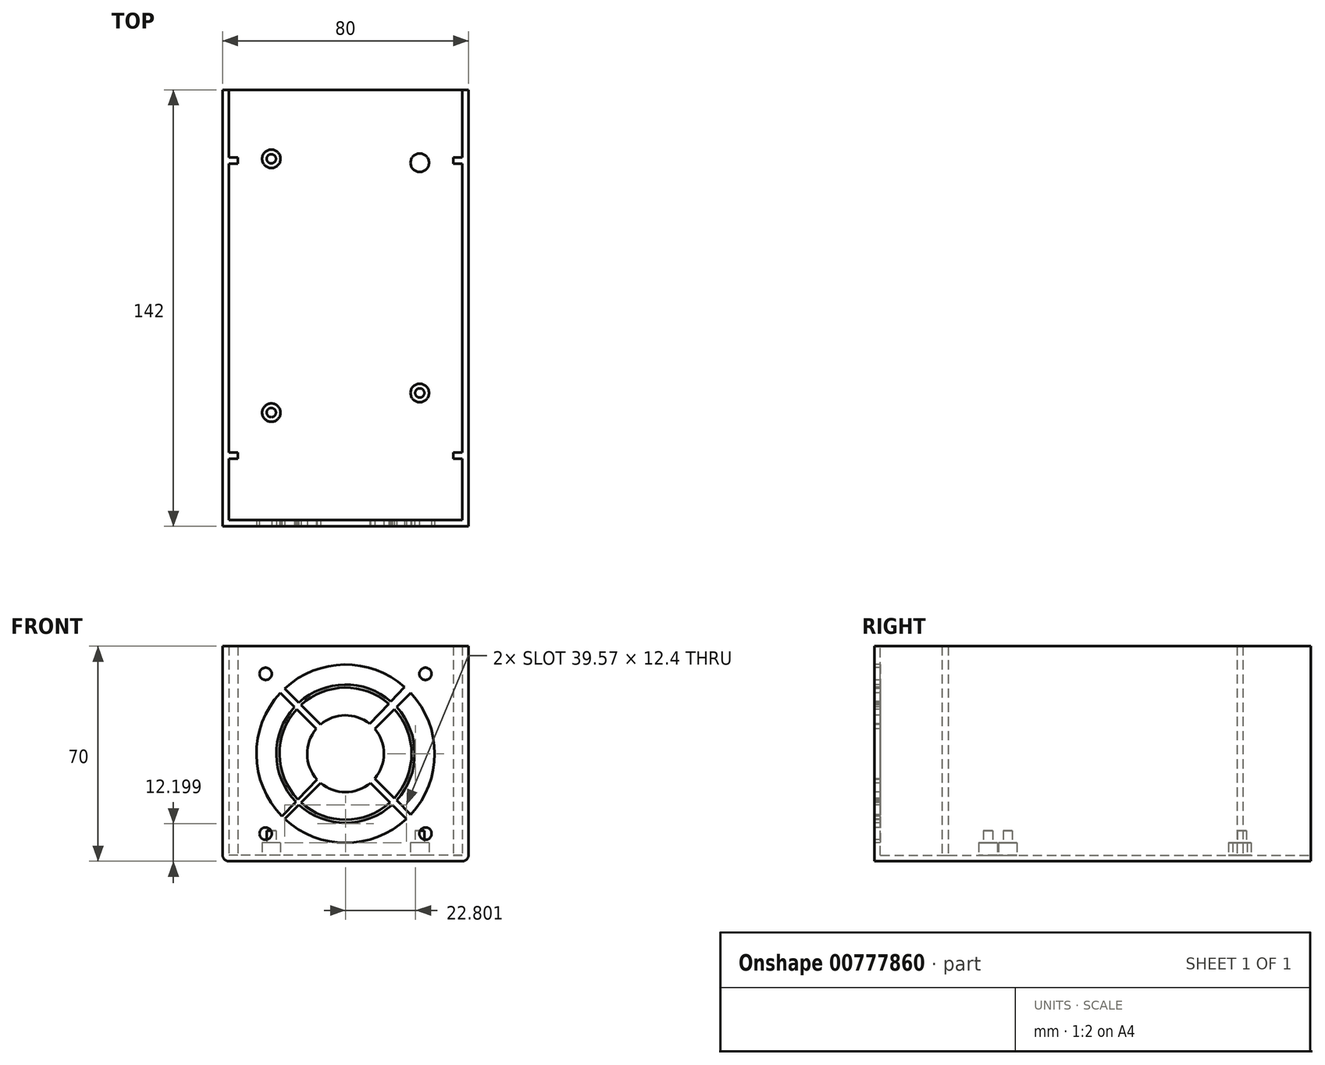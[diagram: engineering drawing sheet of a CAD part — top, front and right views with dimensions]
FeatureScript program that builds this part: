
annotation { "Feature Type Name" : "Feature", "Feature Type Description" : "" }
export const myFeature = defineFeature(function(context is Context, id is Id, definition is map)
    precondition{}
    {
        {
            var Q0;
            Q0=qCreatedBy(makeId("Front.planeOp"),FACE);
            var sketch = newSketch(context, id + "F0", { "sketchPlane" : qUnion([Q0])});
            skLineSegment(sketch, "E0.bottom", {"start": v(-40, 0) * mm, "end": v(40, 0) * mm});
            skLineSegment(sketch, "E0.top", {"start": v(-40, 70) * mm, "end": v(40, 70) * mm});
            skLineSegment(sketch, "E0.left", {"start": v(-40, 0) * mm, "end": v(-40, 70) * mm});
            skLineSegment(sketch, "E0.right", {"start": v(40, 0) * mm, "end": v(40, 70) * mm});
            skPoint(sketch, "E0.middle", {"position": v(0, 35) * mm});
            skSolve(sketch);
        }
        {
            var Q0;
            Q0 = qSketchRegion(id + "F0", true);
            extrude(context, id + "F1", {"entities" : qUnion([Q0]), "depth" : 2 * mm, "offsetDistance" : 25 * mm});
        }
        {
            var Q0;
            Q0=qCreatedBy(makeId("Top.planeOp"),FACE);
            var sketch = newSketch(context, id + "F2", { "sketchPlane" : qUnion([Q0])});
            skLineSegment(sketch, "E1.bottom", {"start": v(40, 0) * mm, "end": v(-40, 0) * mm});
            skLineSegment(sketch, "E1.top", {"start": v(40, 140) * mm, "end": v(-40, 140) * mm});
            skLineSegment(sketch, "E1.left", {"start": v(40, 0) * mm, "end": v(40, 140) * mm});
            skLineSegment(sketch, "E1.right", {"start": v(-40, 0) * mm, "end": v(-40, 140) * mm});
            skPoint(sketch, "E1.middle", {"position": v(0, 70) * mm});
            skSolve(sketch);
        }
        {
            var Q0;
            Q0 = qSketchRegion(id + "F2", true);
            extrude(context, id + "F3", {"entities" : qUnion([Q0]), "operationType" : NewBodyOperationType.ADD, "depth" : 2 * mm, "offsetDistance" : 25 * mm});
        }
        {
            var Q0;
            Q0=makeQuery(id+"F3.boolean.opBoolean","MERGE",FACE,{"derivedFrom":[makeQuery(id+"F1.opExtrude","SWEPT_FACE",FACE,{"disambiguationData":[OSD([sQuery(id+"F0.wireOp",EDGE,"E0.left")])]}),makeQuery(id+"F3.opExtrude","SWEPT_FACE",FACE,{"disambiguationData":[OSD([sQuery(id+"F2.wireOp",EDGE,"E1.right")])]})]});
            var sketch = newSketch(context, id + "F4", { "sketchPlane" : qUnion([Q0])});
            skLineSegment(sketch, "E2.bottom", {"start": v(-140, 2) * mm, "end": v(0, 2) * mm});
            skLineSegment(sketch, "E2.top", {"start": v(-140, 70) * mm, "end": v(0, 70) * mm});
            skLineSegment(sketch, "E2.left", {"start": v(-140, 2) * mm, "end": v(-140, 70) * mm});
            skLineSegment(sketch, "E2.right", {"start": v(0, 2) * mm, "end": v(0, 70) * mm});
            skSolve(sketch);
        }
        {
            var Q0;
            Q0=makeQuery(id+"F4.imprint","IMPRINT",FACE,{"disambiguationData":[TD([[makeQuery(id+"F4.imprint","IMPRINT",EDGE,{"derivedFrom":sQuery(id+"F4.wireOp",EDGE,"E2.bottom")}),-1.0]])]});
            extrude(context, id + "F5", {"entities" : qUnion([Q0]), "operationType" : NewBodyOperationType.ADD, "oppositeDirection" : true, "depth" : 2 * mm, "offsetDistance" : 25 * mm});
        }
        {
            var Q0;
            Q0=makeQuery(id+"F3.boolean.opBoolean","MERGE",FACE,{"derivedFrom":[makeQuery(id+"F1.opExtrude","SWEPT_FACE",FACE,{"disambiguationData":[OSD([sQuery(id+"F0.wireOp",EDGE,"E0.right")])]}),makeQuery(id+"F3.opExtrude","SWEPT_FACE",FACE,{"disambiguationData":[OSD([sQuery(id+"F2.wireOp",EDGE,"E1.left")])]})]});
            var sketch = newSketch(context, id + "F6", { "sketchPlane" : qUnion([Q0])});
            skLineSegment(sketch, "E3.bottom", {"start": v(140, 2) * mm, "end": v(0, 2) * mm});
            skLineSegment(sketch, "E3.top", {"start": v(140, 70) * mm, "end": v(0, 70) * mm});
            skLineSegment(sketch, "E3.left", {"start": v(140, 2) * mm, "end": v(140, 70) * mm});
            skLineSegment(sketch, "E3.right", {"start": v(0, 2) * mm, "end": v(0, 70) * mm});
            skSolve(sketch);
        }
        {
            var Q0;
            Q0=makeQuery(id+"F6.imprint","IMPRINT",FACE,{"disambiguationData":[TD([[makeQuery(id+"F6.imprint","IMPRINT",EDGE,{"derivedFrom":sQuery(id+"F6.wireOp",EDGE,"E3.bottom")}),1.0]])]});
            extrude(context, id + "F7", {"entities" : qUnion([Q0]), "operationType" : NewBodyOperationType.ADD, "oppositeDirection" : true, "depth" : 2 * mm, "offsetDistance" : 25 * mm});
        }
        {
            var Q0;
            Q0=makeQuery(id+"F1.opExtrude","CAP_FACE",FACE,{"disambiguationData":[OSD([sQuery(id+"F0.wireOp",EDGE,"E0.bottom"),sQuery(id+"F0.wireOp",EDGE,"E0.top"),sQuery(id+"F0.wireOp",EDGE,"E0.left"),sQuery(id+"F0.wireOp",EDGE,"E0.right")])],"isStart":false});
            var sketch = newSketch(context, id + "F8", { "sketchPlane" : qUnion([Q0])});
            skArc(sketch, "E4", {"start": v(-21.2, 54.79) * mm, "mid": v(-29, 34.6) * mm, "end": v(-20.66, 14.64) * mm});
            skPoint(sketch, "E4.centerSnap0", {"position": v(-40, 35) * mm});
            skLineSegment(sketch, "E5.bottom", {"start": v(-30, 65) * mm, "end": v(30, 65) * mm});
            skLineSegment(sketch, "E5.top", {"start": v(-30, 5) * mm, "end": v(30, 5) * mm});
            skLineSegment(sketch, "E5.left", {"start": v(-30, 65) * mm, "end": v(-30, 5) * mm});
            skLineSegment(sketch, "E5.right", {"start": v(30, 65) * mm, "end": v(30, 5) * mm});
            skCircle(sketch, "E6", {"center": v(-26, 61) * mm, "radius": 2 * mm});
            skCircle(sketch, "E7", {"center": v(26, 61) * mm, "radius": 2 * mm});
            skCircle(sketch, "E8", {"center": v(-26, 9) * mm, "radius": 2 * mm});
            skCircle(sketch, "E9", {"center": v(26, 9) * mm, "radius": 2 * mm});
            skLineSegment(sketch, "E10", {"start": v(-25.48, 59.07) * mm, "end": v(-25.48, 59.07) * mm});
            skLineSegment(sketch, "E11", {"start": v(-19.79, 56.2) * mm, "end": v(-15.19, 51.6) * mm});
            skLineSegment(sketch, "E12", {"start": v(-20.66, 14.64) * mm, "end": v(-16.18, 19.37) * mm});
            skLineSegment(sketch, "E13.trimOffspring", {"start": v(-21.2, 54.79) * mm, "end": v(-16.6, 50.19) * mm});
            skLineSegment(sketch, "E14.trimOffspring", {"start": v(-19.79, 13.8) * mm, "end": v(-15.19, 18.4) * mm});
            skArc(sketch, "E15", {"start": v(-8.1, 25.48) * mm, "mid": v(0, 22.5) * mm, "end": v(8.1, 25.48) * mm});
            skArc(sketch, "E16", {"start": v(-15.9, 49.48) * mm, "mid": v(-21.5, 34.7) * mm, "end": v(-15.5, 20.1) * mm});
            skArc(sketch, "E17", {"start": v(-16.6, 50.19) * mm, "mid": v(-22.5, 34.7) * mm, "end": v(-16.18, 19.37) * mm});
            skLineSegment(sketch, "E18.trimOffspring", {"start": v(-15.9, 49.48) * mm, "end": v(-9.52, 43.1) * mm});
            skLineSegment(sketch, "E19.trimOffspring", {"start": v(-14.48, 50.9) * mm, "end": v(-8.1, 44.52) * mm});
            skLineSegment(sketch, "E20.trimOffspring", {"start": v(14.73, 52) * mm, "end": v(19.2, 56.73) * mm});
            skLineSegment(sketch, "E21.trimOffspring", {"start": v(16.6, 50.19) * mm, "end": v(21.2, 54.79) * mm});
            skLineSegment(sketch, "E22.trimOffspring", {"start": v(16.6, 19.81) * mm, "end": v(21.2, 15.21) * mm});
            skLineSegment(sketch, "E23.trimOffspring", {"start": v(15.19, 18.4) * mm, "end": v(19.79, 13.8) * mm});
            skArc(sketch, "E24.trimOffspring", {"start": v(15.9, 20.52) * mm, "mid": v(21.5, 35) * mm, "end": v(15.9, 49.48) * mm});
            skArc(sketch, "E25.trimOffspring", {"start": v(16.6, 19.81) * mm, "mid": v(22.5, 35) * mm, "end": v(16.6, 50.19) * mm});
            skLineSegment(sketch, "E26.trimOffspring", {"start": v(-14.48, 19.1) * mm, "end": v(-8.1, 25.48) * mm});
            skLineSegment(sketch, "E27.trimOffspring", {"start": v(-15.5, 20.1) * mm, "end": v(-9.3, 26.64) * mm});
            skArc(sketch, "E28.trimOffspring", {"start": v(-15.19, 18.4) * mm, "mid": v(0, 12.5) * mm, "end": v(15.19, 18.4) * mm});
            skArc(sketch, "E29.trimOffspring", {"start": v(-14.48, 19.1) * mm, "mid": v(0, 13.5) * mm, "end": v(14.48, 19.1) * mm});
            skArc(sketch, "E30.trimOffspring", {"start": v(9.52, 26.9) * mm, "mid": v(12.5, 35) * mm, "end": v(9.52, 43.1) * mm});
            skLineSegment(sketch, "E31.trimOffspring", {"start": v(9.52, 26.9) * mm, "end": v(15.9, 20.52) * mm});
            skLineSegment(sketch, "E32.trimOffspring", {"start": v(8.1, 25.48) * mm, "end": v(14.48, 19.1) * mm});
            skLineSegment(sketch, "E33.trimOffspring", {"start": v(9.52, 43.1) * mm, "end": v(15.9, 49.48) * mm});
            skLineSegment(sketch, "E34.trimOffspring", {"start": v(7.84, 44.73) * mm, "end": v(14.04, 51.28) * mm});
            skArc(sketch, "E35.trimOffspring", {"start": v(14.04, 51.28) * mm, "mid": v(-0.3, 56.5) * mm, "end": v(-14.48, 50.9) * mm});
            skArc(sketch, "E36.trimOffspring", {"start": v(14.73, 52) * mm, "mid": v(-0.3, 57.5) * mm, "end": v(-15.19, 51.6) * mm});
            skArc(sketch, "E37.trimOffspring", {"start": v(7.84, 44.73) * mm, "mid": v(-0.17, 47.5) * mm, "end": v(-8.1, 44.52) * mm});
            skArc(sketch, "E38.trimOffspring", {"start": v(-9.52, 43.1) * mm, "mid": v(-12.5, 34.83) * mm, "end": v(-9.3, 26.64) * mm});
            skArc(sketch, "E39.trimOffspring", {"start": v(19.2, 56.73) * mm, "mid": v(-0.4, 64) * mm, "end": v(-19.79, 56.2) * mm});
            skArc(sketch, "E40.trimOffspring", {"start": v(21.2, 15.21) * mm, "mid": v(29, 35) * mm, "end": v(21.2, 54.79) * mm});
            skArc(sketch, "E41.trimOffspring", {"start": v(-19.79, 13.8) * mm, "mid": v(0, 6) * mm, "end": v(19.79, 13.8) * mm});
            skSolve(sketch);
        }
        {
            var Q0;
            Q0=makeQuery(id+"F8.imprint","IMPRINT",FACE,{"disambiguationData":[TD([[makeQuery(id+"F8.imprint","IMPRINT",EDGE,{"derivedFrom":sQuery(id+"F8.wireOp",EDGE,"E16")}),1.0]])]});
            var Q1;
            Q1=makeQuery(id+"F8.imprint","IMPRINT",FACE,{"disambiguationData":[TD([[makeQuery(id+"F8.imprint","IMPRINT",EDGE,{"derivedFrom":sQuery(id+"F8.wireOp",EDGE,"E4")}),1.0]])]});
            var Q2;
            Q2=makeQuery(id+"F8.imprint","IMPRINT",FACE,{"disambiguationData":[TD([[makeQuery(id+"F8.imprint","IMPRINT",EDGE,{"derivedFrom":sQuery(id+"F8.wireOp",EDGE,"E6")}),1.0]])]});
            var Q3;
            Q3=makeQuery(id+"F8.imprint","IMPRINT",FACE,{"disambiguationData":[TD([[makeQuery(id+"F8.imprint","IMPRINT",EDGE,{"derivedFrom":sQuery(id+"F8.wireOp",EDGE,"E11")}),1.0]])]});
            var Q4;
            Q4=makeQuery(id+"F8.imprint","IMPRINT",FACE,{"disambiguationData":[TD([[makeQuery(id+"F8.imprint","IMPRINT",EDGE,{"derivedFrom":sQuery(id+"F8.wireOp",EDGE,"E19.trimOffspring")}),1.0]])]});
            var Q5;
            Q5=makeQuery(id+"F8.imprint","IMPRINT",FACE,{"disambiguationData":[TD([[makeQuery(id+"F8.imprint","IMPRINT",EDGE,{"derivedFrom":sQuery(id+"F8.wireOp",EDGE,"E24.trimOffspring")}),1.0]])]});
            var Q6;
            Q6=makeQuery(id+"F8.imprint","IMPRINT",FACE,{"disambiguationData":[TD([[makeQuery(id+"F8.imprint","IMPRINT",EDGE,{"derivedFrom":sQuery(id+"F8.wireOp",EDGE,"E21.trimOffspring")}),-1.0]])]});
            var Q7;
            Q7=makeQuery(id+"F8.imprint","IMPRINT",FACE,{"disambiguationData":[TD([[makeQuery(id+"F8.imprint","IMPRINT",EDGE,{"derivedFrom":sQuery(id+"F8.wireOp",EDGE,"E7")}),1.0]])]});
            var Q8;
            Q8=makeQuery(id+"F8.imprint","IMPRINT",FACE,{"disambiguationData":[TD([[makeQuery(id+"F8.imprint","IMPRINT",EDGE,{"derivedFrom":sQuery(id+"F8.wireOp",EDGE,"E9")}),1.0]])]});
            var Q9;
            Q9=makeQuery(id+"F8.imprint","IMPRINT",FACE,{"disambiguationData":[TD([[makeQuery(id+"F8.imprint","IMPRINT",EDGE,{"derivedFrom":sQuery(id+"F8.wireOp",EDGE,"E14.trimOffspring")}),-1.0]])]});
            var Q10;
            Q10=makeQuery(id+"F8.imprint","IMPRINT",FACE,{"disambiguationData":[TD([[makeQuery(id+"F8.imprint","IMPRINT",EDGE,{"derivedFrom":sQuery(id+"F8.wireOp",EDGE,"E15")}),-1.0]])]});
            var Q11;
            Q11=makeQuery(id+"F8.imprint","IMPRINT",FACE,{"disambiguationData":[TD([[makeQuery(id+"F8.imprint","IMPRINT",EDGE,{"derivedFrom":sQuery(id+"F8.wireOp",EDGE,"E8")}),1.0]])]});
            extrude(context, id + "F9", {"entities" : qUnion([Q0, Q1, Q2, Q3, Q4, Q5, Q6, Q7, Q8, Q9, Q10, Q11]), "operationType" : NewBodyOperationType.REMOVE, "oppositeDirection" : true, "depth" : 2 * mm, "offsetDistance" : 25 * mm});
        }
        {
            var Q0;
            Q0=makeQuery(id+"F3.boolean.opBoolean","MERGE",EDGE,{"derivedFrom":[makeQuery(id+"F1.opExtrude","SWEPT_EDGE",EDGE,{"disambiguationData":[OSD([sQuery(id+"F0.wireOp",EDGE,"E0.bottom"),sQuery(id+"F0.wireOp",EDGE,"E0.right")])]}),makeQuery(id+"F3.opExtrude","CAP_EDGE",EDGE,{"disambiguationData":[OSD([sQuery(id+"F2.wireOp",EDGE,"E1.left")])],"isStart":true})]});
            var Q1;
            Q1=makeQuery(id+"F3.boolean.opBoolean","MERGE",EDGE,{"derivedFrom":[makeQuery(id+"F1.opExtrude","SWEPT_EDGE",EDGE,{"disambiguationData":[OSD([sQuery(id+"F0.wireOp",EDGE,"E0.bottom"),sQuery(id+"F0.wireOp",EDGE,"E0.left")])]}),makeQuery(id+"F3.opExtrude","CAP_EDGE",EDGE,{"disambiguationData":[OSD([sQuery(id+"F2.wireOp",EDGE,"E1.right")])],"isStart":true})]});
            fillet(context, id + "F10", {"entities" : qUnion([Q0, Q1]), "radius" : 2 * mm, "tangentPropagation" : true, "allowEdgeOverflow" : false});
        }
        {
            var Q0;
            Q0=makeQuery(id+"F3.opExtrude","CAP_FACE",FACE,{"disambiguationData":[OSD([sQuery(id+"F2.wireOp",EDGE,"E1.bottom"),sQuery(id+"F2.wireOp",EDGE,"E1.top"),sQuery(id+"F2.wireOp",EDGE,"E1.left"),sQuery(id+"F2.wireOp",EDGE,"E1.right")])],"isStart":false});
            var sketch = newSketch(context, id + "F11", { "sketchPlane" : qUnion([Q0])});
            skLineSegment(sketch, "E42.bottom", {"start": v(-26.65, 131.6) * mm, "end": v(26.65, 131.6) * mm});
            skLineSegment(sketch, "E42.top", {"start": v(-26.65, 30) * mm, "end": v(26.65, 30) * mm});
            skLineSegment(sketch, "E42.left", {"start": v(-26.65, 131.6) * mm, "end": v(-26.65, 30) * mm});
            skLineSegment(sketch, "E42.right", {"start": v(26.65, 131.6) * mm, "end": v(26.65, 30) * mm});
            skPoint(sketch, "E42.middle", {"position": v(0, 80.8) * mm});
            skPoint(sketch, "E42.middle.positionSnap0", {"position": v(0, 140) * mm});
            skPoint(sketch, "E42.middle.positionSnap1", {"position": v(-33, 80.8) * mm});
            skPoint(sketch, "E42.centerSnap0", {"position": v(0, 140) * mm});
            skPoint(sketch, "E42.centerSnap1", {"position": v(-33, 80.8) * mm});
            skCircle(sketch, "E43", {"center": v(-24.15, 35) * mm, "radius": 1.5 * mm});
            skCircle(sketch, "E44", {"center": v(24.15, 41.4) * mm, "radius": 1.5 * mm});
            skCircle(sketch, "E45", {"center": v(-24.15, 117.6) * mm, "radius": 1.5 * mm});
            skCircle(sketch, "E46", {"center": v(24.15, 116.3) * mm, "radius": 1.5 * mm});
            skCircle(sketch, "E47", {"center": v(-24.15, 117.6) * mm, "radius": 3 * mm});
            skCircle(sketch, "E48", {"center": v(24.15, 116.3) * mm, "radius": 3 * mm});
            skCircle(sketch, "E49", {"center": v(-24.15, 35) * mm, "radius": 3 * mm});
            skCircle(sketch, "E50", {"center": v(24.15, 41.4) * mm, "radius": 3 * mm});
            skSolve(sketch);
        }
        {
            var Q0;
            Q0=makeQuery(id+"F11.imprint","IMPRINT",FACE,{"disambiguationData":[TD([[makeQuery(id+"F11.imprint","IMPRINT",EDGE,{"derivedFrom":sQuery(id+"F11.wireOp",EDGE,"E45")}),-1.0]])]});
            var Q1;
            Q1=makeQuery(id+"F11.imprint","IMPRINT",FACE,{"disambiguationData":[TD([[makeQuery(id+"F11.imprint","IMPRINT",EDGE,{"derivedFrom":sQuery(id+"F11.wireOp",EDGE,"E46")}),-1.0]])]});
            var Q2;
            Q2=makeQuery(id+"F11.imprint","IMPRINT",FACE,{"disambiguationData":[TD([[makeQuery(id+"F11.imprint","IMPRINT",EDGE,{"derivedFrom":sQuery(id+"F11.wireOp",EDGE,"E43")}),-1.0]])]});
            var Q3;
            Q3=makeQuery(id+"F11.imprint","IMPRINT",FACE,{"disambiguationData":[TD([[makeQuery(id+"F11.imprint","IMPRINT",EDGE,{"derivedFrom":sQuery(id+"F11.wireOp",EDGE,"E44")}),-1.0]])]});
            var Q4;
            Q4=makeQuery(id+"F11.imprint","IMPRINT",FACE,{"disambiguationData":[TD([[makeQuery(id+"F11.imprint","IMPRINT",EDGE,{"derivedFrom":sQuery(id+"F11.wireOp",EDGE,"E46")}),1.0]])]});
            var Q5;
            {var subQ0=sQuery(id+"F11.wireOp",EDGE,"E48");var subQ1=sQuery(id+"F11.wireOp",EDGE,"E42.right");var subQ2=makeQuery(id+"F11.imprint","INTERSECT",VERTEX,{"disambiguationData":[OD(0.0)],"derivedFrom":[subQ1,subQ0]});Q5=makeQuery(id+"F11.imprint","IMPRINT",FACE,{"disambiguationData":[TD([[makeQuery(id+"F11.imprint","IMPRINT",EDGE,{"disambiguationData":[TD([[subQ2,-1.0]])],"derivedFrom":subQ1}),1.0]])]});}
            var Q6;
            {var subQ0=sQuery(id+"F11.wireOp",EDGE,"E47");var subQ1=sQuery(id+"F11.wireOp",EDGE,"E42.left");var subQ2=makeQuery(id+"F11.imprint","INTERSECT",VERTEX,{"disambiguationData":[OD(0.0)],"derivedFrom":[subQ1,subQ0]});Q6=makeQuery(id+"F11.imprint","IMPRINT",FACE,{"disambiguationData":[TD([[makeQuery(id+"F11.imprint","IMPRINT",EDGE,{"disambiguationData":[TD([[subQ2,-1.0]])],"derivedFrom":subQ1}),-1.0]])]});}
            var Q7;
            {var subQ0=sQuery(id+"F11.wireOp",EDGE,"E50");var subQ1=sQuery(id+"F11.wireOp",EDGE,"E42.right");var subQ2=makeQuery(id+"F11.imprint","INTERSECT",VERTEX,{"disambiguationData":[OD(0.0)],"derivedFrom":[subQ1,subQ0]});Q7=makeQuery(id+"F11.imprint","IMPRINT",FACE,{"disambiguationData":[TD([[makeQuery(id+"F11.imprint","IMPRINT",EDGE,{"disambiguationData":[TD([[subQ2,-1.0]])],"derivedFrom":subQ1}),1.0]])]});}
            var Q8;
            {var subQ0=sQuery(id+"F11.wireOp",EDGE,"E49");var subQ1=sQuery(id+"F11.wireOp",EDGE,"E42.left");var subQ2=makeQuery(id+"F11.imprint","INTERSECT",VERTEX,{"disambiguationData":[OD(0.0)],"derivedFrom":[subQ1,subQ0]});Q8=makeQuery(id+"F11.imprint","IMPRINT",FACE,{"disambiguationData":[TD([[makeQuery(id+"F11.imprint","IMPRINT",EDGE,{"disambiguationData":[TD([[subQ2,-1.0]])],"derivedFrom":subQ1}),-1.0]])]});}
            extrude(context, id + "F12", {"entities" : qUnion([Q0, Q1, Q2, Q3, Q4, Q5, Q6, Q7, Q8]), "operationType" : NewBodyOperationType.ADD, "depth" : 4 * mm, "offsetDistance" : 25 * mm});
        }
        {
            var Q0;
            Q0=makeQuery(id+"F11.imprint","IMPRINT",FACE,{"disambiguationData":[TD([[makeQuery(id+"F11.imprint","IMPRINT",EDGE,{"derivedFrom":sQuery(id+"F11.wireOp",EDGE,"E43")}),1.0]])]});
            var Q1;
            Q1=makeQuery(id+"F11.imprint","IMPRINT",FACE,{"disambiguationData":[TD([[makeQuery(id+"F11.imprint","IMPRINT",EDGE,{"derivedFrom":sQuery(id+"F11.wireOp",EDGE,"E45")}),1.0]])]});
            extrude(context, id + "F13", {"entities" : qUnion([Q0, Q1]), "operationType" : NewBodyOperationType.ADD, "depth" : 8 * mm, "offsetDistance" : 25 * mm});
        }
        {
            var Q0;
            Q0=makeQuery(id+"F11.imprint","IMPRINT",FACE,{"disambiguationData":[TD([[makeQuery(id+"F11.imprint","IMPRINT",EDGE,{"derivedFrom":sQuery(id+"F11.wireOp",EDGE,"E44")}),1.0]])]});
            extrude(context, id + "F14", {"entities" : qUnion([Q0]), "operationType" : NewBodyOperationType.ADD, "depth" : 8 * mm, "offsetDistance" : 25 * mm});
        }
        {
            var Q0;
            Q0=makeQuery(id+"F7.opExtrude","CAP_FACE",FACE,{"disambiguationData":[OSD([sQuery(id+"F6.wireOp",EDGE,"E3.bottom"),sQuery(id+"F6.wireOp",EDGE,"E3.top"),sQuery(id+"F6.wireOp",EDGE,"E3.left"),sQuery(id+"F6.wireOp",EDGE,"E3.right")])],"isStart":false});
            var sketch = newSketch(context, id + "F15", { "sketchPlane" : qUnion([Q0])});
            skLineSegment(sketch, "E51.bottom", {"start": v(-118, 70) * mm, "end": v(-116, 70) * mm});
            skLineSegment(sketch, "E51.top", {"start": v(-118, 2) * mm, "end": v(-116, 2) * mm});
            skLineSegment(sketch, "E51.left", {"start": v(-118, 70) * mm, "end": v(-118, 2) * mm});
            skLineSegment(sketch, "E51.right", {"start": v(-116, 70) * mm, "end": v(-116, 2) * mm});
            skLineSegment(sketch, "E52.bottom", {"start": v(-22, 70) * mm, "end": v(-20, 70) * mm});
            skLineSegment(sketch, "E52.top", {"start": v(-22, 2) * mm, "end": v(-20, 2) * mm});
            skLineSegment(sketch, "E52.left", {"start": v(-22, 70) * mm, "end": v(-22, 2) * mm});
            skLineSegment(sketch, "E52.right", {"start": v(-20, 70) * mm, "end": v(-20, 2) * mm});
            skSolve(sketch);
        }
        {
            var Q0;
            Q0=makeQuery(id+"F15.imprint","IMPRINT",FACE,{"disambiguationData":[TD([[makeQuery(id+"F15.imprint","IMPRINT",EDGE,{"derivedFrom":sQuery(id+"F15.wireOp",EDGE,"E51.bottom")}),-1.0]])]});
            var Q1;
            Q1=makeQuery(id+"F15.imprint","IMPRINT",FACE,{"disambiguationData":[TD([[makeQuery(id+"F15.imprint","IMPRINT",EDGE,{"derivedFrom":sQuery(id+"F15.wireOp",EDGE,"E52.bottom")}),-1.0]])]});
            extrude(context, id + "F16", {"entities" : qUnion([Q0, Q1]), "operationType" : NewBodyOperationType.ADD, "depth" : 3 * mm, "offsetDistance" : 25 * mm});
        }
        {
            var Q0;
            Q0=makeQuery(id+"F5.opExtrude","CAP_FACE",FACE,{"disambiguationData":[OSD([sQuery(id+"F4.wireOp",EDGE,"E2.bottom"),sQuery(id+"F4.wireOp",EDGE,"E2.top"),sQuery(id+"F4.wireOp",EDGE,"E2.left"),sQuery(id+"F4.wireOp",EDGE,"E2.right")])],"isStart":false});
            var sketch = newSketch(context, id + "F17", { "sketchPlane" : qUnion([Q0])});
            skLineSegment(sketch, "E53.bottom", {"start": v(20, 70) * mm, "end": v(22, 70) * mm});
            skLineSegment(sketch, "E53.top", {"start": v(20, 2) * mm, "end": v(22, 2) * mm});
            skLineSegment(sketch, "E53.left", {"start": v(20, 70) * mm, "end": v(20, 2) * mm});
            skLineSegment(sketch, "E53.right", {"start": v(22, 70) * mm, "end": v(22, 2) * mm});
            skLineSegment(sketch, "E54.bottom", {"start": v(116, 70) * mm, "end": v(118, 70) * mm});
            skLineSegment(sketch, "E54.top", {"start": v(116, 2) * mm, "end": v(118, 2) * mm});
            skLineSegment(sketch, "E54.left", {"start": v(116, 70) * mm, "end": v(116, 2) * mm});
            skLineSegment(sketch, "E54.right", {"start": v(118, 70) * mm, "end": v(118, 2) * mm});
            skSolve(sketch);
        }
        {
            var Q0;
            Q0=makeQuery(id+"F17.imprint","IMPRINT",FACE,{"disambiguationData":[TD([[makeQuery(id+"F17.imprint","IMPRINT",EDGE,{"derivedFrom":sQuery(id+"F17.wireOp",EDGE,"E53.bottom")}),1.0]])]});
            var Q1;
            Q1=makeQuery(id+"F17.imprint","IMPRINT",FACE,{"disambiguationData":[TD([[makeQuery(id+"F17.imprint","IMPRINT",EDGE,{"derivedFrom":sQuery(id+"F17.wireOp",EDGE,"E54.bottom")}),1.0]])]});
            extrude(context, id + "F18", {"entities" : qUnion([Q0, Q1]), "operationType" : NewBodyOperationType.ADD, "depth" : 3 * mm, "offsetDistance" : 25 * mm});
        }
    });
